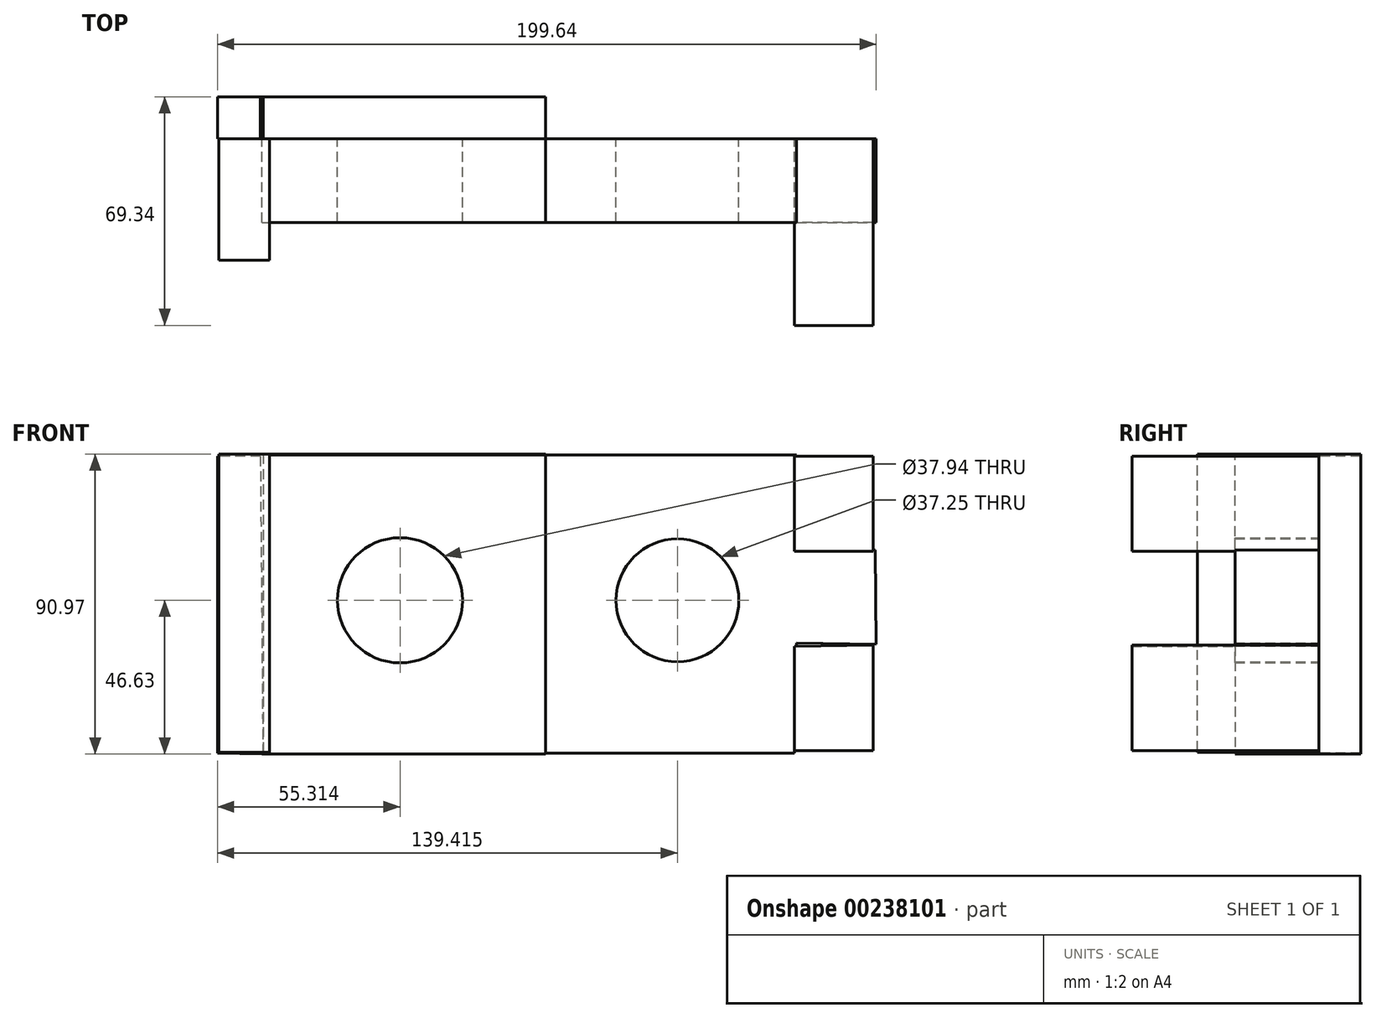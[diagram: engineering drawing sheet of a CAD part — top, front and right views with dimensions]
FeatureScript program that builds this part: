
annotation { "Feature Type Name" : "Feature", "Feature Type Description" : "" }
export const myFeature = defineFeature(function(context is Context, id is Id, definition is map)
    precondition{}
    {
        {
            var Q0;
            Q0=qCreatedBy(makeId("Front.planeOp"),FACE);
            var sketch = newSketch(context, id + "F0", { "sketchPlane" : qUnion([Q0])});
            skLineSegment(sketch, "E0", {"start": v(-85.5, 44.34) * mm, "end": v(0, 44.34) * mm});
            skLineSegment(sketch, "E1", {"start": v(-85.5, 44.34) * mm, "end": v(-85.5, -46.63) * mm});
            skLineSegment(sketch, "E2", {"start": v(-85.5, -46.63) * mm, "end": v(0, -46.63) * mm});
            skLineSegment(sketch, "E3", {"start": v(0, -46.63) * mm, "end": v(0, 44.34) * mm});
            skSolve(sketch);
        }
        {
            var Q0;
            Q0 = qSketchRegion(id + "F0", true);
            extrude(context, id + "F1", {"entities" : qUnion([Q0]), "oppositeDirection" : true, "depth" : 12.7 * mm});
        }
        {
            var Q0;
            Q0=qCreatedBy(makeId("Front.planeOp"),FACE);
            var sketch = newSketch(context, id + "F2", { "sketchPlane" : qUnion([Q0])});
            skLineSegment(sketch, "E4", {"start": v(0, 44.01) * mm, "end": v(76.18, 44.01) * mm});
            skLineSegment(sketch, "E5", {"start": v(0, -46.3) * mm, "end": v(75.53, -46.3) * mm});
            skLineSegment(sketch, "E6", {"start": v(76.18, 44.01) * mm, "end": v(76.18, 15.21) * mm});
            skLineSegment(sketch, "E7", {"start": v(75.53, -46.3) * mm, "end": v(76.18, -12.93) * mm});
            skLineSegment(sketch, "E8", {"start": v(76.18, 15.21) * mm, "end": v(99.95, 15.21) * mm});
            skLineSegment(sketch, "E9", {"start": v(76.18, -12.93) * mm, "end": v(100.26, -13.4) * mm});
            skLineSegment(sketch, "E10", {"start": v(100.26, -13.4) * mm, "end": v(99.95, 15.21) * mm});
            skLineSegment(sketch, "E11", {"start": v(0, 44.01) * mm, "end": v(0, -46.3) * mm});
            skSolve(sketch);
        }
        {
            var Q0;
            Q0 = qSketchRegion(id + "F2", true);
            extrude(context, id + "F3", {"entities" : qUnion([Q0]), "depth" : 25.4 * mm});
        }
        {
            var Q0;
            Q0=qCreatedBy(makeId("Front.planeOp"),FACE);
            var sketch = newSketch(context, id + "F4", { "sketchPlane" : qUnion([Q0])});
            skLineSegment(sketch, "E12", {"start": v(0, 44.01) * mm, "end": v(-85.88, 44.01) * mm});
            skLineSegment(sketch, "E13", {"start": v(-85.88, 44.01) * mm, "end": v(-85.88, -46.63) * mm});
            skLineSegment(sketch, "E14", {"start": v(-85.88, -46.63) * mm, "end": v(0, -46.63) * mm});
            skLineSegment(sketch, "E15", {"start": v(0, -46.63) * mm, "end": v(0, 44.01) * mm});
            skSolve(sketch);
        }
        {
            var Q0;
            Q0 = qSketchRegion(id + "F4", true);
            extrude(context, id + "F5", {"entities" : qUnion([Q0]), "depth" : 25.4 * mm});
        }
        {
            var Q0;
            Q0=qCreatedBy(makeId("Front.planeOp"),FACE);
            var sketch = newSketch(context, id + "F6", { "sketchPlane" : qUnion([Q0])});
            skLineSegment(sketch, "E16", {"start": v(75.45, 43.68) * mm, "end": v(99.34, 43.68) * mm});
            skLineSegment(sketch, "E17", {"start": v(99.34, 43.68) * mm, "end": v(99.34, 14.89) * mm});
            skLineSegment(sketch, "E18", {"start": v(75.45, 43.68) * mm, "end": v(75.45, 14.89) * mm});
            skLineSegment(sketch, "E19", {"start": v(75.45, 14.89) * mm, "end": v(99.34, 14.89) * mm});
            skLineSegment(sketch, "E20", {"start": v(75.45, -45.65) * mm, "end": v(99.34, -45.65) * mm});
            skLineSegment(sketch, "E21", {"start": v(99.34, -45.65) * mm, "end": v(99.34, -13.58) * mm});
            skLineSegment(sketch, "E22", {"start": v(75.45, -45.65) * mm, "end": v(75.45, -13.9) * mm});
            skLineSegment(sketch, "E23", {"start": v(75.45, -13.9) * mm, "end": v(99.34, -13.58) * mm});
            skSolve(sketch);
        }
        {
            var Q0;
            Q0 = qSketchRegion(id + "F6", true);
            extrude(context, id + "F7", {"entities" : qUnion([Q0]), "operationType" : NewBodyOperationType.ADD, "depth" : 56.64 * mm});
        }
        {
            var Q0;
            Q0=qCreatedBy(makeId("Front.planeOp"),FACE);
            var sketch = newSketch(context, id + "F8", { "sketchPlane" : qUnion([Q0])});
            skLineSegment(sketch, "E24", {"start": v(-86.4, 43.68) * mm, "end": v(-99.38, 43.68) * mm});
            skLineSegment(sketch, "E25", {"start": v(-99.38, 43.68) * mm, "end": v(-99.38, -46.3) * mm});
            skLineSegment(sketch, "E26", {"start": v(-85.64, -46.63) * mm, "end": v(-99.38, -46.3) * mm});
            skLineSegment(sketch, "E27", {"start": v(-86.4, 43.68) * mm, "end": v(-85.64, -46.63) * mm});
            skSolve(sketch);
        }
        {
            var Q0;
            Q0 = qSketchRegion(id + "F8", true);
            extrude(context, id + "F9", {"entities" : qUnion([Q0]), "operationType" : NewBodyOperationType.ADD, "oppositeDirection" : true, "depth" : 12.7 * mm});
        }
        {
            var Q0;
            Q0=qCreatedBy(makeId("Front.planeOp"),FACE);
            var sketch = newSketch(context, id + "F10", { "sketchPlane" : qUnion([Q0])});
            skLineSegment(sketch, "E28", {"start": v(-83.66, 44.34) * mm, "end": v(-99.04, 44.34) * mm});
            skLineSegment(sketch, "E29", {"start": v(-99.04, 44.34) * mm, "end": v(-99.04, -46.12) * mm});
            skLineSegment(sketch, "E30", {"start": v(-99.04, -46.12) * mm, "end": v(-83.67, -46.12) * mm});
            skLineSegment(sketch, "E31", {"start": v(-83.67, -46.12) * mm, "end": v(-83.66, 44.34) * mm});
            skSolve(sketch);
        }
        {
            var Q0;
            Q0 = qSketchRegion(id + "F10", true);
            extrude(context, id + "F11", {"entities" : qUnion([Q0]), "depth" : 36.83 * mm});
        }
        {
            var Q0;
            Q0=qCreatedBy(makeId("Front.planeOp"),FACE);
            var sketch = newSketch(context, id + "F12", { "sketchPlane" : qUnion([Q0])});
            skCircle(sketch, "E32", {"center": v(40.03, 0) * mm, "radius": 18.62 * mm});
            skCircle(sketch, "E33", {"center": v(-44.07, 0) * mm, "radius": 18.97 * mm});
            skSolve(sketch);
        }
        {
            var Q0;
            Q0 = qSketchRegion(id + "F12", true);
            extrude(context, id + "F13", {"entities" : qUnion([Q0]), "operationType" : NewBodyOperationType.REMOVE, "depth" : 96.27 * mm});
        }
    });
